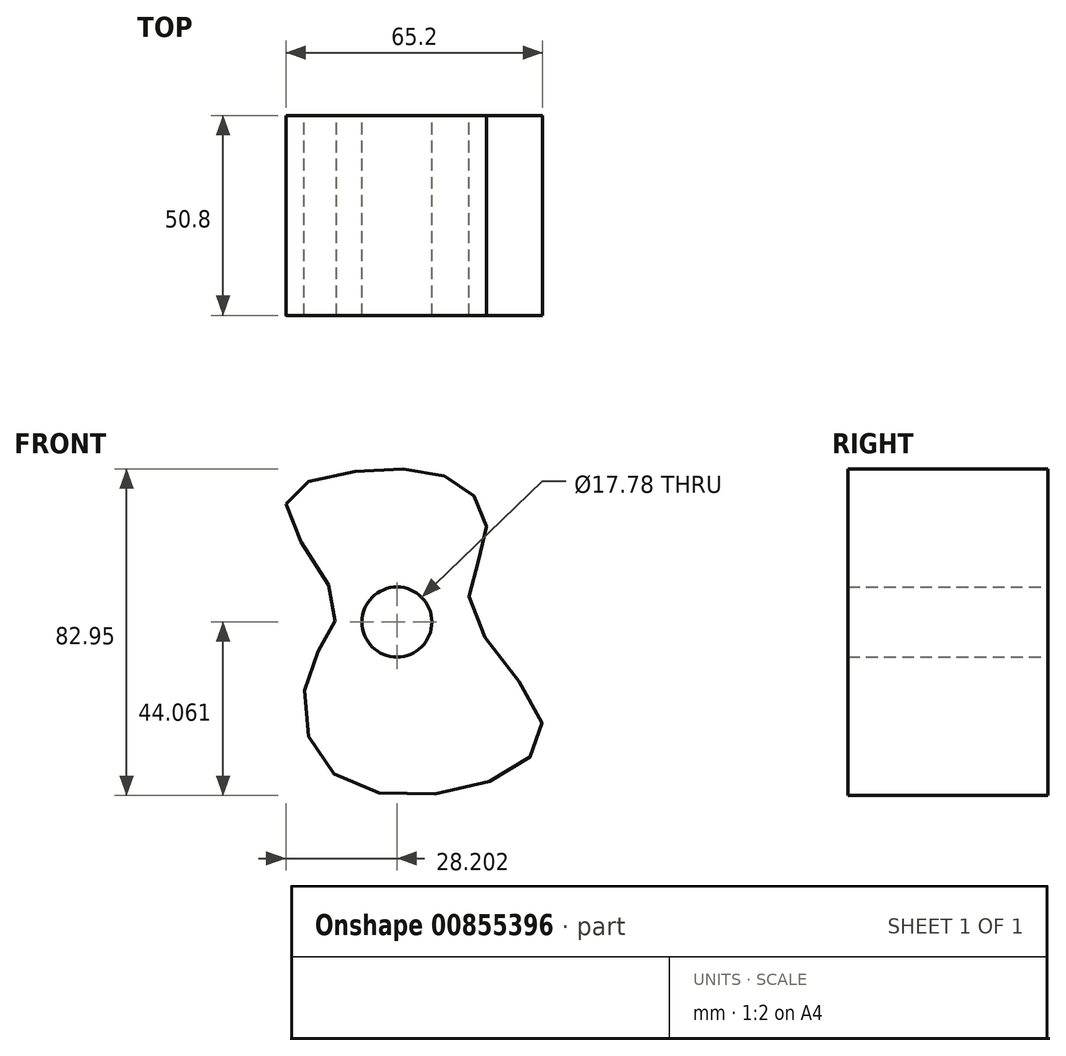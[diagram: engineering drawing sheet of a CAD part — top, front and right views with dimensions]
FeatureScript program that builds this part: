
annotation { "Feature Type Name" : "Feature", "Feature Type Description" : "" }
export const myFeature = defineFeature(function(context is Context, id is Id, definition is map)
    precondition{}
    {
        {
            var Q0;
            Q0=qCreatedBy(makeId("Front.planeOp"),FACE);
            var sketch = newSketch(context, id + "F0", { "sketchPlane" : qUnion([Q0])});
            skFitSpline(sketch, "E0", {"points": [v(-46.84, 56.26) * mm, v(-34.11, 30.81) * mm, v(-40.52, 15.17) * mm, v(-36.37, -10.84) * mm, v(0, -15.74) * mm, v(18.28, 0) * mm, v(0, 29.68) * mm, v(3.96, 48.15) * mm, v(-2.45, 61.35) * mm, v(-27.52, 64.74) * mm, v(-46.84, 56.26) * mm]});
            skCircle(sketch, "E1", {"center": v(-18.66, 26.3) * mm, "radius": 8.9 * mm});
            skSolve(sketch);
        }
        {
            var Q0;
            Q0=makeQuery(id+"F0.imprint","IMPRINT",FACE,{"disambiguationData":[TD([[makeQuery(id+"F0.imprint","IMPRINT",EDGE,{"derivedFrom":sQuery(id+"F0.wireOp",EDGE,"E0")}),1.0]])]});
            extrude(context, id + "F1", {"entities" : qUnion([Q0]), "depth" : 50.8 * mm, "offsetDistance" : 25.4 * mm});
        }
    });
